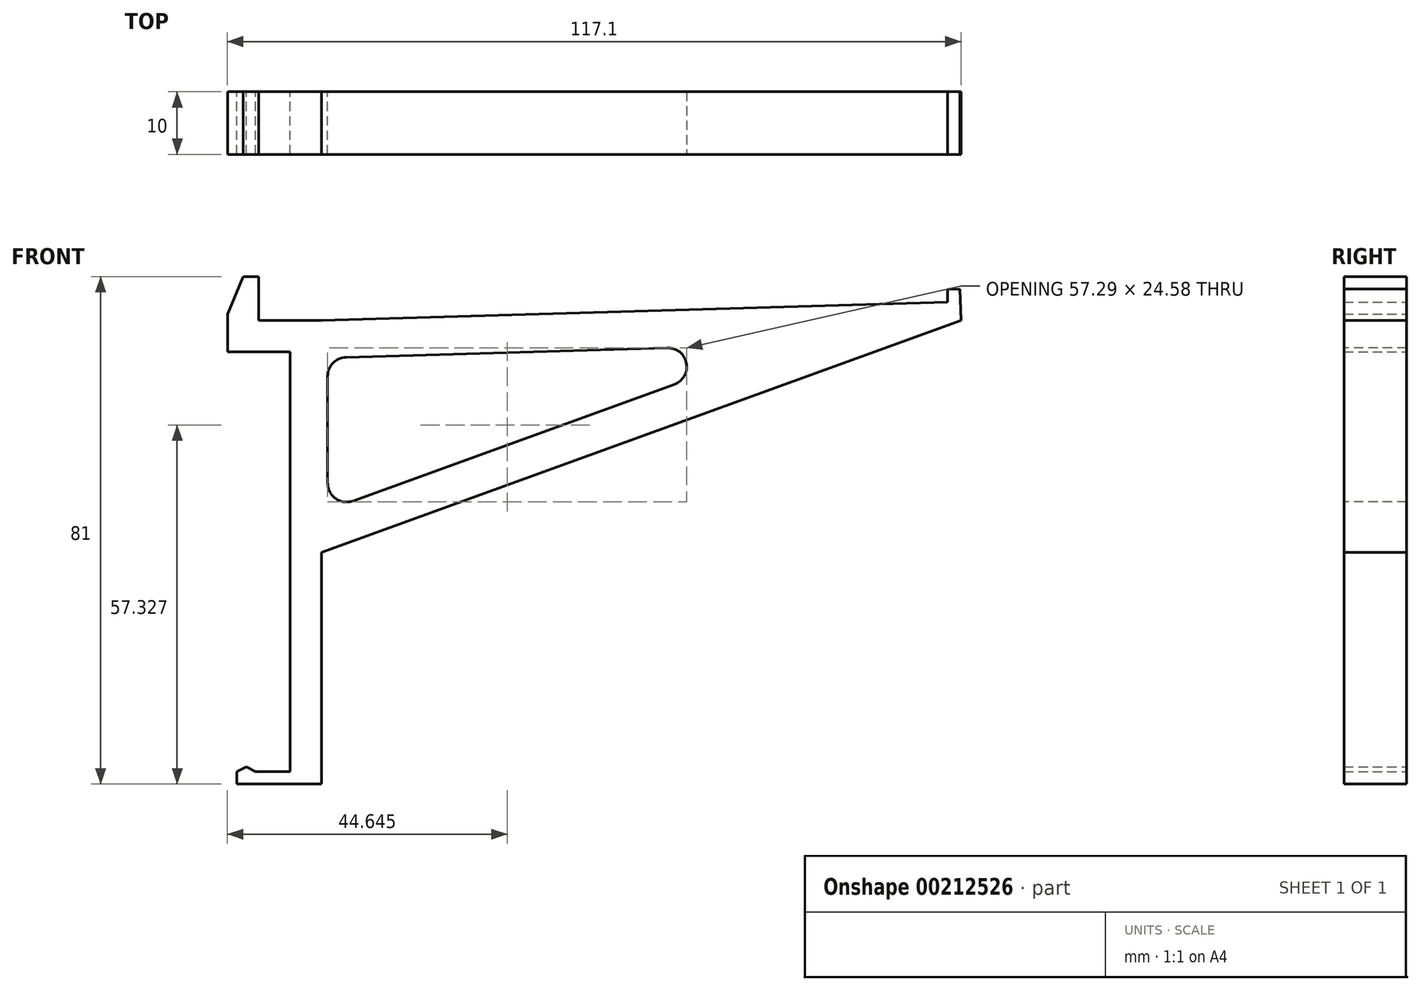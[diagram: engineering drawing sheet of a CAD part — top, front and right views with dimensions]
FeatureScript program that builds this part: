
annotation { "Feature Type Name" : "Feature", "Feature Type Description" : "" }
export const myFeature = defineFeature(function(context is Context, id is Id, definition is map)
    precondition{}
    {
        {
            var Q0;
            Q0=qCreatedBy(makeId("Front.planeOp"),FACE);
            var sketch = newSketch(context, id + "F0", { "sketchPlane" : qUnion([Q0])});
            skLineSegment(sketch, "E0", {"start": v(3.84, -35.6) * mm, "end": v(3.84, 31.4) * mm});
            skLineSegment(sketch, "E1", {"start": v(3.84, 31.4) * mm, "end": v(-6.16, 31.4) * mm});
            skLineSegment(sketch, "E2", {"start": v(-6.16, 31.4) * mm, "end": v(-6.16, 37.4) * mm});
            skLineSegment(sketch, "E3", {"start": v(-3.67, 43.4) * mm, "end": v(-1.17, 43.4) * mm});
            skLineSegment(sketch, "E4", {"start": v(-1.17, 43.4) * mm, "end": v(-1.17, 36.4) * mm});
            skLineSegment(sketch, "E5", {"start": v(-1.17, 36.4) * mm, "end": v(8.84, 36.4) * mm});
            skLineSegment(sketch, "E6", {"start": v(8.84, -0.6) * mm, "end": v(8.84, -37.6) * mm});
            skLineSegment(sketch, "E7", {"start": v(8.84, -37.6) * mm, "end": v(-4.66, -37.6) * mm});
            skLineSegment(sketch, "E8", {"start": v(-4.66, -37.6) * mm, "end": v(-4.66, -35.6) * mm});
            skLineSegment(sketch, "E9", {"start": v(-1.66, -35.6) * mm, "end": v(3.84, -35.6) * mm});
            skLineSegment(sketch, "E10", {"start": v(-1.66, -35.6) * mm, "end": v(-3.16, -34.84) * mm});
            skLineSegment(sketch, "E11", {"start": v(-3.16, -34.84) * mm, "end": v(-4.66, -35.6) * mm});
            skLineSegment(sketch, "E12", {"start": v(-3.67, 43.4) * mm, "end": v(-6.16, 37.4) * mm});
            skPoint(sketch, "E13.orphan", {"position": v(-6.16, 43.4) * mm});
            skLineSegment(sketch, "E14", {"start": v(8.84, 36.4) * mm, "end": v(108.8, 39.34) * mm});
            skLineSegment(sketch, "E15", {"start": v(108.8, 39.34) * mm, "end": v(108.8, 41.34) * mm});
            skLineSegment(sketch, "E16", {"start": v(108.8, 41.34) * mm, "end": v(110.8, 41.4) * mm});
            skLineSegment(sketch, "E17", {"start": v(110.8, 41.4) * mm, "end": v(110.94, 36.4) * mm});
            skLineSegment(sketch, "E18", {"start": v(110.94, 36.4) * mm, "end": v(8.84, -0.6) * mm});
            skLineSegment(sketch, "E19.0", {"start": v(9.84, 30.43) * mm, "end": v(82.77, 32.58) * mm});
            skLineSegment(sketch, "E20.trimOffspring", {"start": v(9.84, 6.15) * mm, "end": v(9.84, 30.43) * mm});
            skLineSegment(sketch, "E21.trimOffspring", {"start": v(82.77, 32.58) * mm, "end": v(9.84, 6.15) * mm});
            skSolve(sketch);
        }
        {
            var Q0;
            Q0=makeQuery(id+"F0.imprint","IMPRINT",FACE,{"disambiguationData":[TD([[makeQuery(id+"F0.imprint","IMPRINT",EDGE,{"derivedFrom":sQuery(id+"F0.wireOp",EDGE,"E0")}),-1.0]])]});
            extrude(context, id + "F1", {"entities" : qUnion([Q0]), "endBound" : BoundingType.SYMMETRIC, "depth" : 10 * mm});
        }
        {
            var Q0;
            Q0=makeQuery(id+"F1.opExtrude","SWEPT_EDGE",EDGE,{"disambiguationData":[OSD([sQuery(id+"F0.wireOp",EDGE,"E19.0"),sQuery(id+"F0.wireOp",EDGE,"E21.trimOffspring")])]});
            var Q1;
            Q1=makeQuery(id+"F1.opExtrude","SWEPT_EDGE",EDGE,{"disambiguationData":[OSD([sQuery(id+"F0.wireOp",EDGE,"E19.0"),sQuery(id+"F0.wireOp",EDGE,"E20.trimOffspring")])]});
            var Q2;
            Q2=makeQuery(id+"F1.opExtrude","SWEPT_EDGE",EDGE,{"disambiguationData":[OSD([sQuery(id+"F0.wireOp",EDGE,"E20.trimOffspring"),sQuery(id+"F0.wireOp",EDGE,"E21.trimOffspring")])]});
            fillet(context, id + "F2", {"entities" : qUnion([Q0, Q1, Q2]), "radius" : 3 * mm, "tangentPropagation" : true, "allowEdgeOverflow" : false});
        }
    });
